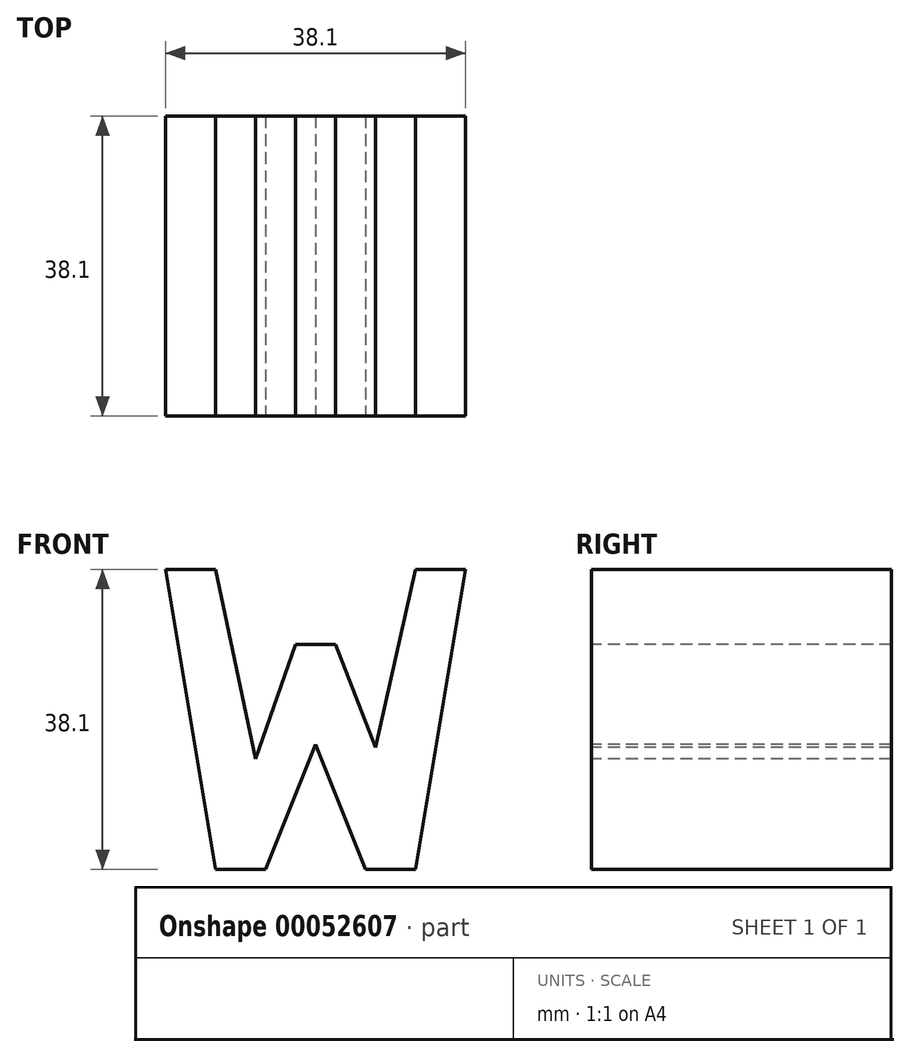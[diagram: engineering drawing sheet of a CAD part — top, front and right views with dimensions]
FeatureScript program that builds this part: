
annotation { "Feature Type Name" : "Feature", "Feature Type Description" : "" }
export const myFeature = defineFeature(function(context is Context, id is Id, definition is map)
    precondition{}
    {
        {
            var Q0;
            Q0=qCreatedBy(makeId("Front.planeOp"),FACE);
            var sketch = newSketch(context, id + "F0", { "sketchPlane" : qUnion([Q0])});
            skLineSegment(sketch, "E0.bottom", {"start": v(0, 0) * mm, "end": v(38.1, 0) * mm});
            skLineSegment(sketch, "E0.top", {"start": v(0, 38.1) * mm, "end": v(38.1, 38.1) * mm});
            skLineSegment(sketch, "E0.left", {"start": v(0, 0) * mm, "end": v(0, 38.1) * mm});
            skLineSegment(sketch, "E0.right", {"start": v(38.1, 0) * mm, "end": v(38.1, 38.1) * mm});
            skSolve(sketch);
        }
        {
            var Q0;
            Q0=makeQuery(id+"F0.imprint","IMPRINT",FACE,{"disambiguationData":[TD([[makeQuery(id+"F0.imprint","IMPRINT",EDGE,{"derivedFrom":sQuery(id+"F0.wireOp",EDGE,"E0.bottom")}),1.0]])]});
            extrude(context, id + "F1", {"entities" : qUnion([Q0]), "depth" : 38.1 * mm});
        }
        {
            var Q0;
            Q0=makeQuery(id+"F1.opExtrude","SWEPT_FACE",FACE,{"disambiguationData":[OSD([sQuery(id+"F0.wireOp",EDGE,"E0.right")])]});
            var sketch = newSketch(context, id + "F2", { "sketchPlane" : qUnion([Q0])});
            skLineSegment(sketch, "E1", {"start": v(-38.1, 38.1) * mm, "end": v(-33.34, 0) * mm});
            skLineSegment(sketch, "E2", {"start": v(-35, 38.1) * mm, "end": v(-30.56, 16.4) * mm});
            skLineSegment(sketch, "E3", {"start": v(-30.56, 16.4) * mm, "end": v(-25.5, 23.89) * mm});
            skLineSegment(sketch, "E4", {"start": v(-25.5, 23.89) * mm, "end": v(-17.85, 23.89) * mm});
            skLineSegment(sketch, "E5", {"start": v(-17.85, 23.89) * mm, "end": v(-13.15, 16.49) * mm});
            skLineSegment(sketch, "E6", {"start": v(-13.15, 16.49) * mm, "end": v(-5.57, 38.1) * mm});
            skLineSegment(sketch, "E7", {"start": v(0, 38.1) * mm, "end": v(-6.01, 0) * mm});
            skLineSegment(sketch, "E8", {"start": v(-12.71, 0) * mm, "end": v(-20.55, 15.18) * mm});
            skLineSegment(sketch, "E9", {"start": v(-20.55, 15.18) * mm, "end": v(-23.94, 0) * mm});
            skSolve(sketch);
        }
        {
            var Q0;
            Q0=makeQuery(id+"F1.opExtrude","CAP_FACE",FACE,{"disambiguationData":[OSD([sQuery(id+"F0.wireOp",EDGE,"E0.bottom"),sQuery(id+"F0.wireOp",EDGE,"E0.top"),sQuery(id+"F0.wireOp",EDGE,"E0.left"),sQuery(id+"F0.wireOp",EDGE,"E0.right")])],"isStart":false});
            var sketch = newSketch(context, id + "F3", { "sketchPlane" : qUnion([Q0])});
            skLineSegment(sketch, "E10", {"start": v(0, 38.1) * mm, "end": v(6.35, 0) * mm});
            skLineSegment(sketch, "E11", {"start": v(6.35, 38.1) * mm, "end": v(11.43, 14.03) * mm});
            skLineSegment(sketch, "E12", {"start": v(11.43, 14.03) * mm, "end": v(16.52, 28.58) * mm});
            skLineSegment(sketch, "E13", {"start": v(16.52, 28.58) * mm, "end": v(21.6, 28.58) * mm});
            skLineSegment(sketch, "E14", {"start": v(21.6, 28.58) * mm, "end": v(26.68, 15.5) * mm});
            skLineSegment(sketch, "E15", {"start": v(26.68, 15.5) * mm, "end": v(31.76, 38.1) * mm});
            skLineSegment(sketch, "E16", {"start": v(38.1, 38.1) * mm, "end": v(31.75, 0) * mm});
            skLineSegment(sketch, "E17", {"start": v(25.4, 0) * mm, "end": v(19.05, 15.88) * mm});
            skLineSegment(sketch, "E18", {"start": v(19.05, 15.88) * mm, "end": v(12.7, 0) * mm});
            skSolve(sketch);
        }
        {
            var Q0;
            {var subQ0=sQuery(id+"F3.wireOp",EDGE,"E11");Q0=makeQuery(id+"F3.imprint","IMPRINT",FACE,{"disambiguationData":[TD([[makeQuery(id+"F3.imprint","IMPRINT",EDGE,{"derivedFrom":subQ0}),1.0]])]});}
            var Q1;
            {var subQ0=sQuery(id+"F3.wireOp",EDGE,"E10");Q1=makeQuery(id+"F3.imprint","IMPRINT",FACE,{"disambiguationData":[TD([[makeQuery(id+"F3.imprint","IMPRINT",EDGE,{"derivedFrom":subQ0}),-1.0]])]});}
            var Q2;
            {var subQ0=sQuery(id+"F3.wireOp",EDGE,"E17");Q2=makeQuery(id+"F3.imprint","IMPRINT",FACE,{"disambiguationData":[TD([[makeQuery(id+"F3.imprint","IMPRINT",EDGE,{"derivedFrom":subQ0}),1.0]])]});}
            var Q3;
            {var subQ0=sQuery(id+"F3.wireOp",EDGE,"E16");Q3=makeQuery(id+"F3.imprint","IMPRINT",FACE,{"disambiguationData":[TD([[makeQuery(id+"F3.imprint","IMPRINT",EDGE,{"derivedFrom":subQ0}),1.0]])]});}
            extrude(context, id + "F4", {"entities" : qUnion([Q0, Q1, Q2, Q3]), "operationType" : NewBodyOperationType.REMOVE, "oppositeDirection" : true, "depth" : 38.1 * mm});
        }
        {
            var Q0;
            Q0=qCreatedBy(makeId("Right.planeOp"),FACE);
            cPlane(context, id + "F5", {"entities" : qUnion([Q0]), "cplaneType" : CPlaneType.OFFSET, "offset" : 38.1 * mm, "width" : 152.4 * mm, "height" : 152.4 * mm});
        }
    });
